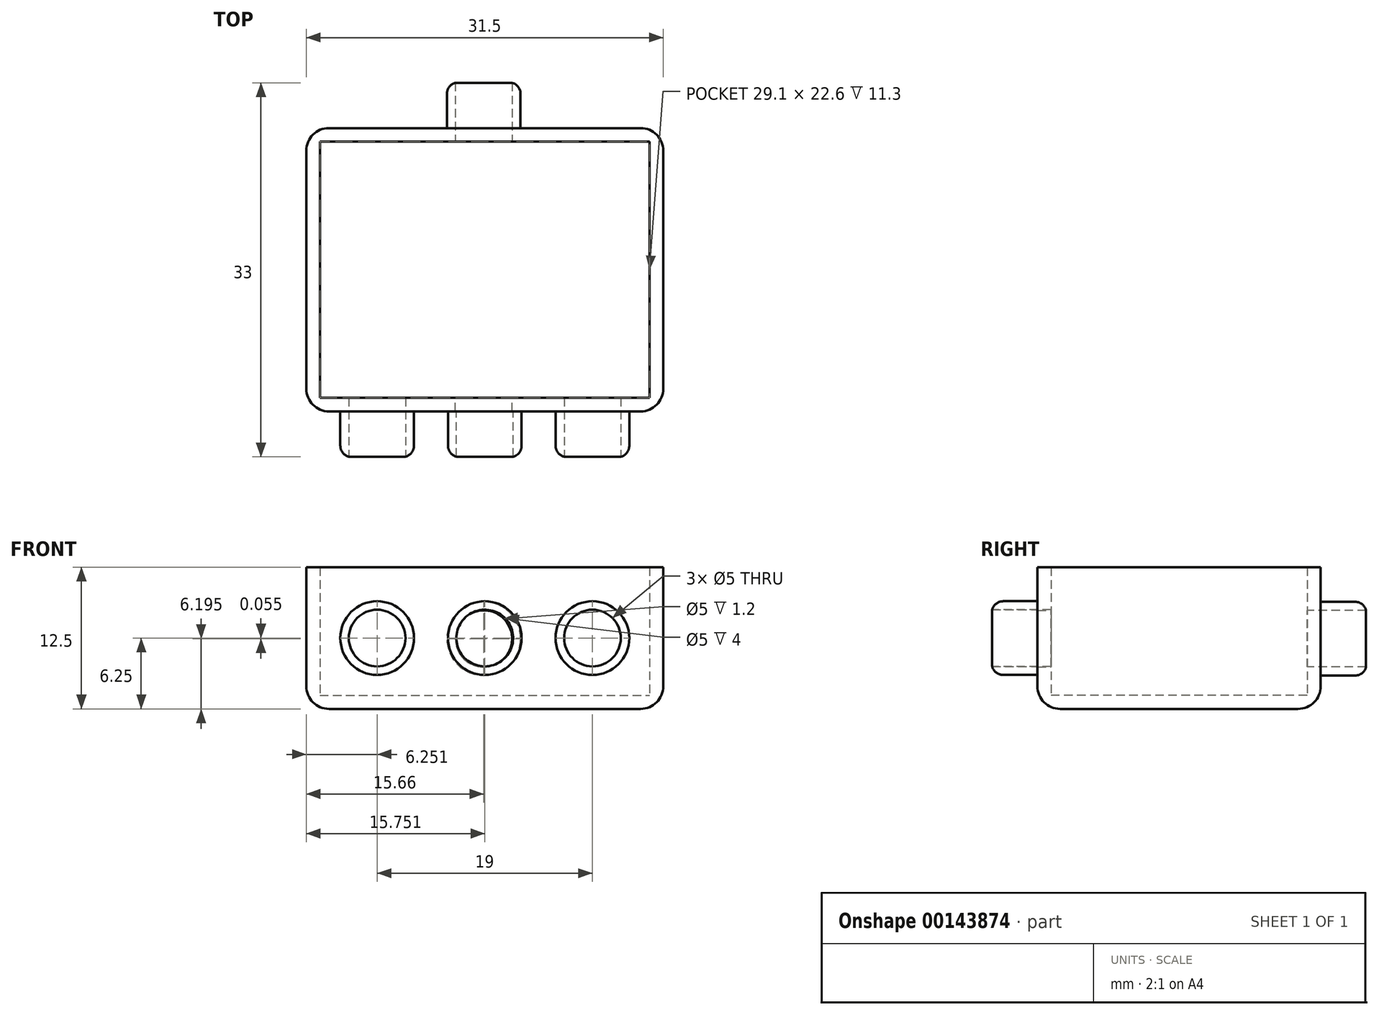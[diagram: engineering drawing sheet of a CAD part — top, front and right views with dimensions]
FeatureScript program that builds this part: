
annotation { "Feature Type Name" : "Feature", "Feature Type Description" : "" }
export const myFeature = defineFeature(function(context is Context, id is Id, definition is map)
    precondition{}
    {
        {
            var Q0;
            Q0=qCreatedBy(makeId("Front.planeOp"),FACE);
            var sketch = newSketch(context, id + "F0", { "sketchPlane" : qUnion([Q0])});
            skCircle(sketch, "E0", {"center": v(-24.4, 20.1) * mm, "radius": 2.5 * mm});
            skCircle(sketch, "E1", {"center": v(-14.9, 20.1) * mm, "radius": 2.5 * mm});
            skCircle(sketch, "E2", {"center": v(-24.4, 20.1) * mm, "radius": 3.25 * mm});
            skCircle(sketch, "E3", {"center": v(-14.9, 20.1) * mm, "radius": 3.25 * mm});
            skLineSegment(sketch, "E4.bottom", {"start": v(-30.65, 26.36) * mm, "end": v(0.85, 26.36) * mm});
            skLineSegment(sketch, "E4.top", {"start": v(-30.65, 13.86) * mm, "end": v(0.85, 13.86) * mm});
            skLineSegment(sketch, "E4.left", {"start": v(-30.65, 26.36) * mm, "end": v(-30.65, 13.86) * mm});
            skLineSegment(sketch, "E4.right", {"start": v(0.85, 26.36) * mm, "end": v(0.85, 13.86) * mm});
            skCircle(sketch, "E5", {"center": v(-5.4, 20.1) * mm, "radius": 2.5 * mm});
            skCircle(sketch, "E6", {"center": v(-5.4, 20.1) * mm, "radius": 3.25 * mm});
            skSolve(sketch);
        }
        {
            var Q0;
            Q0=makeQuery(id+"F0.imprint","IMPRINT",FACE,{"disambiguationData":[TD([[makeQuery(id+"F0.imprint","IMPRINT",EDGE,{"derivedFrom":sQuery(id+"F0.wireOp",EDGE,"E2")}),-1.0]])]});
            var Q1;
            Q1=makeQuery(id+"F0.imprint","IMPRINT",FACE,{"disambiguationData":[TD([[makeQuery(id+"F0.imprint","IMPRINT",EDGE,{"derivedFrom":sQuery(id+"F0.wireOp",EDGE,"E5")}),1.0]])]});
            var Q2;
            Q2=makeQuery(id+"F0.imprint","IMPRINT",FACE,{"disambiguationData":[TD([[makeQuery(id+"F0.imprint","IMPRINT",EDGE,{"derivedFrom":sQuery(id+"F0.wireOp",EDGE,"E5")}),-1.0]])]});
            var Q3;
            Q3=makeQuery(id+"F0.imprint","IMPRINT",FACE,{"disambiguationData":[TD([[makeQuery(id+"F0.imprint","IMPRINT",EDGE,{"derivedFrom":sQuery(id+"F0.wireOp",EDGE,"E1")}),1.0]])]});
            var Q4;
            Q4=makeQuery(id+"F0.imprint","IMPRINT",FACE,{"disambiguationData":[TD([[makeQuery(id+"F0.imprint","IMPRINT",EDGE,{"derivedFrom":sQuery(id+"F0.wireOp",EDGE,"E1")}),-1.0]])]});
            var Q5;
            Q5=makeQuery(id+"F0.imprint","IMPRINT",FACE,{"disambiguationData":[TD([[makeQuery(id+"F0.imprint","IMPRINT",EDGE,{"derivedFrom":sQuery(id+"F0.wireOp",EDGE,"E0")}),1.0]])]});
            var Q6;
            Q6=makeQuery(id+"F0.imprint","IMPRINT",FACE,{"disambiguationData":[TD([[makeQuery(id+"F0.imprint","IMPRINT",EDGE,{"derivedFrom":sQuery(id+"F0.wireOp",EDGE,"E0")}),-1.0]])]});
            extrude(context, id + "F1", {"entities" : qUnion([Q0, Q1, Q2, Q3, Q4, Q5, Q6]), "oppositeDirection" : true, "depth" : 25 * mm});
        }
        {
            var Q0;
            Q0=makeQuery(id+"F1.opExtrude","SWEPT_FACE",FACE,{"disambiguationData":[OSD([sQuery(id+"F0.wireOp",EDGE,"E4.bottom")])]});
            shell(context, id + "F2", {"entities" : qUnion([Q0]), "thickness" : 1.2 * mm});
        }
        {
            var Q0;
            Q0=makeQuery(id+"F1.opExtrude","CAP_FACE",FACE,{"disambiguationData":[OSD([sQuery(id+"F0.wireOp",EDGE,"E4.bottom"),sQuery(id+"F0.wireOp",EDGE,"E4.top"),sQuery(id+"F0.wireOp",EDGE,"E4.left"),sQuery(id+"F0.wireOp",EDGE,"E4.right")])],"isStart":false});
            var sketch = newSketch(context, id + "F3", { "sketchPlane" : qUnion([Q0])});
            skCircle(sketch, "E7", {"center": v(14.99, 20.05) * mm, "radius": 2.5 * mm});
            skCircle(sketch, "E8", {"center": v(14.99, 20.05) * mm, "radius": 3.25 * mm});
            skSolve(sketch);
        }
        {
            var Q0;
            Q0=makeQuery(id+"F3.imprint","IMPRINT",FACE,{"disambiguationData":[TD([[makeQuery(id+"F3.imprint","IMPRINT",EDGE,{"derivedFrom":sQuery(id+"F3.wireOp",EDGE,"E7")}),-1.0]])]});
            extrude(context, id + "F4", {"entities" : qUnion([Q0]), "operationType" : NewBodyOperationType.ADD, "depth" : 4 * mm});
        }
        {
            var Q0;
            Q0=makeQuery(id+"F4.boolean.opBoolean","SPLIT",FACE,{"disambiguationData":[TD([makeQuery(id+"F4.opExtrude","SWEPT_FACE",FACE,{"disambiguationData":[OSD([sQuery(id+"F3.wireOp",EDGE,"E7")])]})])],"derivedFrom":makeQuery(id+"F1.opExtrude","CAP_FACE",FACE,{"disambiguationData":[OSD([sQuery(id+"F0.wireOp",EDGE,"E4.bottom"),sQuery(id+"F0.wireOp",EDGE,"E4.top"),sQuery(id+"F0.wireOp",EDGE,"E4.left"),sQuery(id+"F0.wireOp",EDGE,"E4.right")])],"isStart":false})});
            extrude(context, id + "F5", {"entities" : qUnion([Q0]), "operationType" : NewBodyOperationType.REMOVE, "oppositeDirection" : true, "depth" : 25 * mm});
        }
        {
            var Q0;
            Q0=makeQuery(id+"F0.imprint","IMPRINT",FACE,{"disambiguationData":[TD([[makeQuery(id+"F0.imprint","IMPRINT",EDGE,{"derivedFrom":sQuery(id+"F0.wireOp",EDGE,"E0")}),1.0]])]});
            var Q1;
            Q1=makeQuery(id+"F0.imprint","IMPRINT",FACE,{"disambiguationData":[TD([[makeQuery(id+"F0.imprint","IMPRINT",EDGE,{"derivedFrom":sQuery(id+"F0.wireOp",EDGE,"E5")}),1.0]])]});
            extrude(context, id + "F6", {"entities" : qUnion([Q0, Q1]), "operationType" : NewBodyOperationType.REMOVE, "oppositeDirection" : true, "depth" : 8 * mm});
        }
        {
            var Q0;
            Q0=makeQuery(id+"F0.imprint","IMPRINT",FACE,{"disambiguationData":[TD([[makeQuery(id+"F0.imprint","IMPRINT",EDGE,{"derivedFrom":sQuery(id+"F0.wireOp",EDGE,"E0")}),-1.0]])]});
            var Q1;
            Q1=makeQuery(id+"F0.imprint","IMPRINT",FACE,{"disambiguationData":[TD([[makeQuery(id+"F0.imprint","IMPRINT",EDGE,{"derivedFrom":sQuery(id+"F0.wireOp",EDGE,"E1")}),-1.0]])]});
            var Q2;
            Q2=makeQuery(id+"F0.imprint","IMPRINT",FACE,{"disambiguationData":[TD([[makeQuery(id+"F0.imprint","IMPRINT",EDGE,{"derivedFrom":sQuery(id+"F0.wireOp",EDGE,"E5")}),-1.0]])]});
            extrude(context, id + "F7", {"entities" : qUnion([Q0, Q1, Q2]), "operationType" : NewBodyOperationType.ADD, "depth" : 4 * mm});
        }
        {
            var Q0;
            Q0=makeQuery(id+"F1.opExtrude","SWEPT_EDGE",EDGE,{"disambiguationData":[OSD([sQuery(id+"F0.wireOp",EDGE,"E4.top"),sQuery(id+"F0.wireOp",EDGE,"E4.right")])]});
            var Q1;
            Q1=makeQuery(id+"F1.opExtrude","CAP_EDGE",EDGE,{"disambiguationData":[OSD([sQuery(id+"F0.wireOp",EDGE,"E4.right")])],"isStart":true});
            var Q2;
            Q2=makeQuery(id+"F1.opExtrude","CAP_EDGE",EDGE,{"disambiguationData":[OSD([sQuery(id+"F0.wireOp",EDGE,"E4.top")])],"isStart":true});
            var Q3;
            Q3=makeQuery(id+"F1.opExtrude","SWEPT_EDGE",EDGE,{"disambiguationData":[OSD([sQuery(id+"F0.wireOp",EDGE,"E4.top"),sQuery(id+"F0.wireOp",EDGE,"E4.left")])]});
            var Q4;
            Q4=makeQuery(id+"F1.opExtrude","CAP_EDGE",EDGE,{"disambiguationData":[OSD([sQuery(id+"F0.wireOp",EDGE,"E4.left")])],"isStart":true});
            var Q5;
            Q5=makeQuery(id+"F1.opExtrude","CAP_EDGE",EDGE,{"disambiguationData":[OSD([sQuery(id+"F0.wireOp",EDGE,"E4.left")])],"isStart":false});
            var Q6;
            Q6=makeQuery(id+"F1.opExtrude","CAP_EDGE",EDGE,{"disambiguationData":[OSD([sQuery(id+"F0.wireOp",EDGE,"E4.top")])],"isStart":false});
            var Q7;
            Q7=makeQuery(id+"F1.opExtrude","CAP_EDGE",EDGE,{"disambiguationData":[OSD([sQuery(id+"F0.wireOp",EDGE,"E4.right")])],"isStart":false});
            fillet(context, id + "F8", {"entities" : qUnion([Q0, Q1, Q2, Q3, Q4, Q5, Q6, Q7]), "radius" : 2 * mm, "tangentPropagation" : true, "allowEdgeOverflow" : false});
        }
        {
            var Q0;
            Q0=makeQuery(id+"F7.opExtrude","CAP_EDGE",EDGE,{"disambiguationData":[OSD([sQuery(id+"F0.wireOp",EDGE,"E6")])],"isStart":false});
            var Q1;
            Q1=makeQuery(id+"F7.opExtrude","CAP_EDGE",EDGE,{"disambiguationData":[OSD([sQuery(id+"F0.wireOp",EDGE,"E3")])],"isStart":false});
            var Q2;
            Q2=makeQuery(id+"F7.opExtrude","CAP_EDGE",EDGE,{"disambiguationData":[OSD([sQuery(id+"F0.wireOp",EDGE,"E2")])],"isStart":false});
            var Q3;
            Q3=makeQuery(id+"F4.opExtrude","CAP_EDGE",EDGE,{"disambiguationData":[OSD([sQuery(id+"F3.wireOp",EDGE,"E8")])],"isStart":false});
            fillet(context, id + "F9", {"entities" : qUnion([Q0, Q1, Q2, Q3]), "radius" : 1 * mm, "tangentPropagation" : true, "allowEdgeOverflow" : false});
        }
    });
